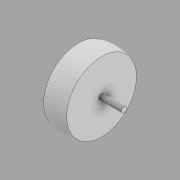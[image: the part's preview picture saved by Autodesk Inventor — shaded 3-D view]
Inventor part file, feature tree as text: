
AUTODESK INVENTOR PART (.ipt)
format: ipt  version: 2021.3 (Build 253353000, 353)  size: 104,448 bytes
history: native  units: in
note: dims shown in document units (in); Inventor stores cm internally (conversion verified against a paired STEP export)
features: sketch x3, other x1, revolve x1, extrude x1, thread x1
ambient origin geometry x8: Origin, YZ Plane, XZ Plane, XY Plane, X Axis, Y Axis, Z Axis, Center Point
bodies: Body1 (feature_tree)
feature tree (7):
  other  "ソリッド1"
  revolve  "回転1"
  sketch  "スケッチ3"
  extrude  "押し出し1"  Depth=3.0906in
  thread  "ねじ1"
  sketch  "スケッチ2"
  sketch  "スケッチ4"
